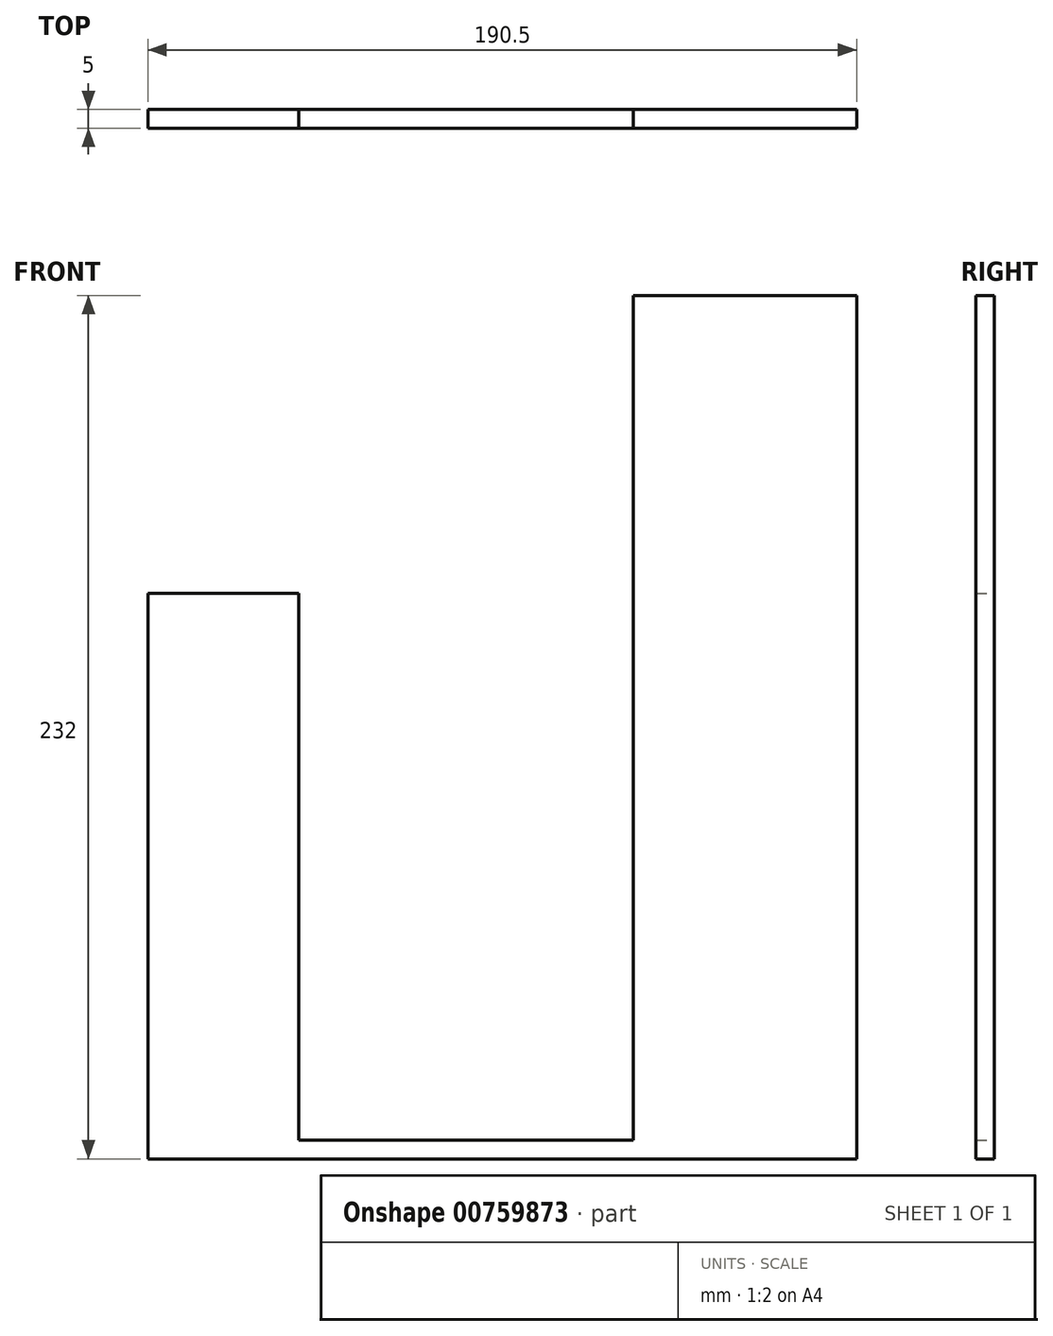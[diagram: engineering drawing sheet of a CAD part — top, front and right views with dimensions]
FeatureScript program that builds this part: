
annotation { "Feature Type Name" : "Feature", "Feature Type Description" : "" }
export const myFeature = defineFeature(function(context is Context, id is Id, definition is map)
    precondition{}
    {
        {
            var Q0;
            Q0=qCreatedBy(makeId("Front.planeOp"),FACE);
            var sketch = newSketch(context, id + "F0", { "sketchPlane" : qUnion([Q0])});
            skLineSegment(sketch, "E0", {"start": v(-95.25, 76) * mm, "end": v(-54.75, 76) * mm});
            skLineSegment(sketch, "E1", {"start": v(-54.75, 76) * mm, "end": v(-54.75, -71) * mm});
            skLineSegment(sketch, "E2", {"start": v(-54.75, -71) * mm, "end": v(35.25, -71) * mm});
            skLineSegment(sketch, "E3", {"start": v(35.25, -71) * mm, "end": v(35.25, 156) * mm});
            skLineSegment(sketch, "E4", {"start": v(35.25, 156) * mm, "end": v(95.25, 156) * mm});
            skLineSegment(sketch, "E5", {"start": v(95.25, 156) * mm, "end": v(95.25, -76) * mm});
            skLineSegment(sketch, "E6", {"start": v(95.25, -76) * mm, "end": v(-95.25, -76) * mm});
            skLineSegment(sketch, "E7", {"start": v(-95.25, -76) * mm, "end": v(-95.25, 76) * mm});
            skSolve(sketch);
        }
        {
            var Q0;
            Q0=makeQuery(id+"F0.imprint","IMPRINT",FACE,{"disambiguationData":[TD([[makeQuery(id+"F0.imprint","IMPRINT",EDGE,{"derivedFrom":sQuery(id+"F0.wireOp",EDGE,"E0")}),-1.0]])]});
            extrude(context, id + "F1", {"entities" : qUnion([Q0]), "depth" : 5 * mm, "offsetDistance" : 25 * mm});
        }
    });
